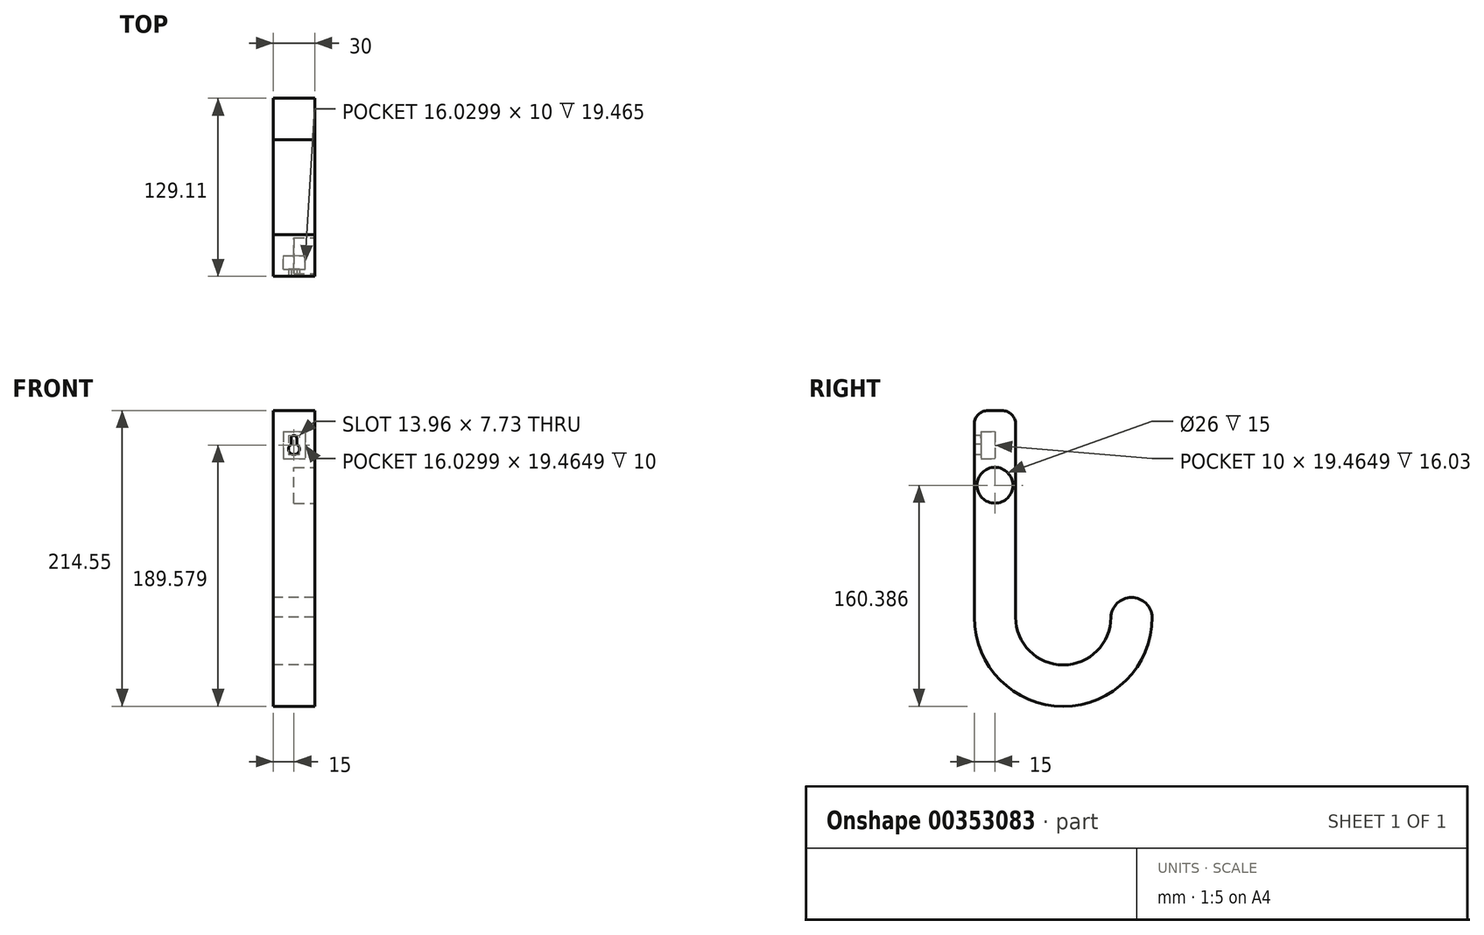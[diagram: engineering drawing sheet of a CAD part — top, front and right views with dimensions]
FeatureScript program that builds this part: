
annotation { "Feature Type Name" : "Feature", "Feature Type Description" : "" }
export const myFeature = defineFeature(function(context is Context, id is Id, definition is map)
    precondition{}
    {
        {
            var Q0;
            Q0=qCreatedBy(makeId("Right.planeOp"),FACE);
            var sketch = newSketch(context, id + "F0", { "sketchPlane" : qUnion([Q0])});
            skLineSegment(sketch, "E0", {"start": v(0, 0) * mm, "end": v(0, 150) * mm});
            skLineSegment(sketch, "E1", {"start": v(0, 150) * mm, "end": v(-30, 150) * mm});
            skLineSegment(sketch, "E2", {"start": v(-30, 150) * mm, "end": v(-30, 0) * mm});
            skArc(sketch, "E3", {"start": v(99.1, 0) * mm, "mid": v(84.1, 14.34) * mm, "end": v(69.1, 0) * mm});
            skArc(sketch, "E4", {"start": v(0, 0) * mm, "mid": v(34.55, -34.55) * mm, "end": v(69.1, 0) * mm});
            skArc(sketch, "E5", {"start": v(-30, 0) * mm, "mid": v(34.55, -64.55) * mm, "end": v(99.1, 0) * mm});
            skSolve(sketch);
        }
        {
            var Q0;
            Q0 = qSketchRegion(id + "F0", true);
            extrude(context, id + "F1", {"entities" : qUnion([Q0]), "depth" : 30 * mm});
        }
        {
            var Q0;
            Q0=makeQuery(id+"F1.opExtrude","CAP_FACE",FACE,{"disambiguationData":[OSD([sQuery(id+"F0.wireOp",EDGE,"E0"),sQuery(id+"F0.wireOp",EDGE,"E1"),sQuery(id+"F0.wireOp",EDGE,"E2"),sQuery(id+"F0.wireOp",EDGE,"E3"),sQuery(id+"F0.wireOp",EDGE,"E4"),sQuery(id+"F0.wireOp",EDGE,"E5")])],"isStart":false});
            var sketch = newSketch(context, id + "F2", { "sketchPlane" : qUnion([Q0])});
            skCircle(sketch, "E6", {"center": v(-15, 95.84) * mm, "radius": 13 * mm});
            skSolve(sketch);
        }
        {
            var Q0;
            Q0=makeQuery(id+"F2.imprint","IMPRINT",FACE,{"disambiguationData":[TD([[makeQuery(id+"F2.imprint","IMPRINT",EDGE,{"derivedFrom":sQuery(id+"F2.wireOp",EDGE,"E6")}),1.0]])]});
            extrude(context, id + "F3", {"entities" : qUnion([Q0]), "operationType" : NewBodyOperationType.REMOVE, "oppositeDirection" : true, "depth" : 15 * mm});
        }
        {
            var Q0;
            Q0=makeQuery(id+"F1.opExtrude","SWEPT_FACE",FACE,{"disambiguationData":[OSD([sQuery(id+"F0.wireOp",EDGE,"E2")])]});
            var sketch = newSketch(context, id + "F4", { "sketchPlane" : qUnion([Q0])});
            skArc(sketch, "E7", {"start": v(13, 125.51) * mm, "mid": v(15, 118.05) * mm, "end": v(17, 125.51) * mm});
            skLineSegment(sketch, "E8", {"start": v(13, 125.51) * mm, "end": v(13, 130.01) * mm});
            skArc(sketch, "E9", {"start": v(17, 130.01) * mm, "mid": v(15, 132.01) * mm, "end": v(13, 130.01) * mm});
            skLineSegment(sketch, "E10", {"start": v(17, 130.01) * mm, "end": v(17, 125.51) * mm});
            skSolve(sketch);
        }
        {
            var Q0;
            Q0 = qSketchRegion(id + "F4", true);
            extrude(context, id + "F5", {"entities" : qUnion([Q0]), "operationType" : NewBodyOperationType.REMOVE, "oppositeDirection" : true, "depth" : 15 * mm});
        }
        {
            var Q0;
            Q0=makeQuery(id+"F5.boolean.opBoolean","COPY",FACE,{"derivedFrom":makeQuery(id+"F5.opExtrude","CAP_FACE",FACE,{"disambiguationData":[OSD([sQuery(id+"F4.wireOp",EDGE,"E7"),sQuery(id+"F4.wireOp",EDGE,"E8"),sQuery(id+"F4.wireOp",EDGE,"E9"),sQuery(id+"F4.wireOp",EDGE,"E10")])],"isStart":false})});
            var sketch = newSketch(context, id + "F6", { "sketchPlane" : qUnion([Q0])});
            skLineSegment(sketch, "E11.bottom", {"start": v(7.25, 134.63) * mm, "end": v(23.28, 134.63) * mm});
            skLineSegment(sketch, "E11.top", {"start": v(7.25, 115.17) * mm, "end": v(23.28, 115.17) * mm});
            skLineSegment(sketch, "E11.left", {"start": v(7.25, 134.63) * mm, "end": v(7.25, 115.17) * mm});
            skLineSegment(sketch, "E11.right", {"start": v(23.28, 134.63) * mm, "end": v(23.28, 115.17) * mm});
            skSolve(sketch);
        }
        {
            var Q0;
            Q0 = qSketchRegion(id + "F6", true);
            extrude(context, id + "F7", {"entities" : qUnion([Q0]), "operationType" : NewBodyOperationType.REMOVE, "depth" : 10 * mm});
        }
        {
            var Q0;
            Q0=makeQuery(id+"F1.opExtrude","SWEPT_EDGE",EDGE,{"disambiguationData":[OSD([sQuery(id+"F0.wireOp",EDGE,"E0"),sQuery(id+"F0.wireOp",EDGE,"E1")])]});
            var Q1;
            Q1=makeQuery(id+"F1.opExtrude","SWEPT_EDGE",EDGE,{"disambiguationData":[OSD([sQuery(id+"F0.wireOp",EDGE,"E1"),sQuery(id+"F0.wireOp",EDGE,"E2")])]});
            fillet(context, id + "F8", {"entities" : qUnion([Q0, Q1]), "radius" : 10 * mm, "tangentPropagation" : true, "allowEdgeOverflow" : false});
        }
    });
